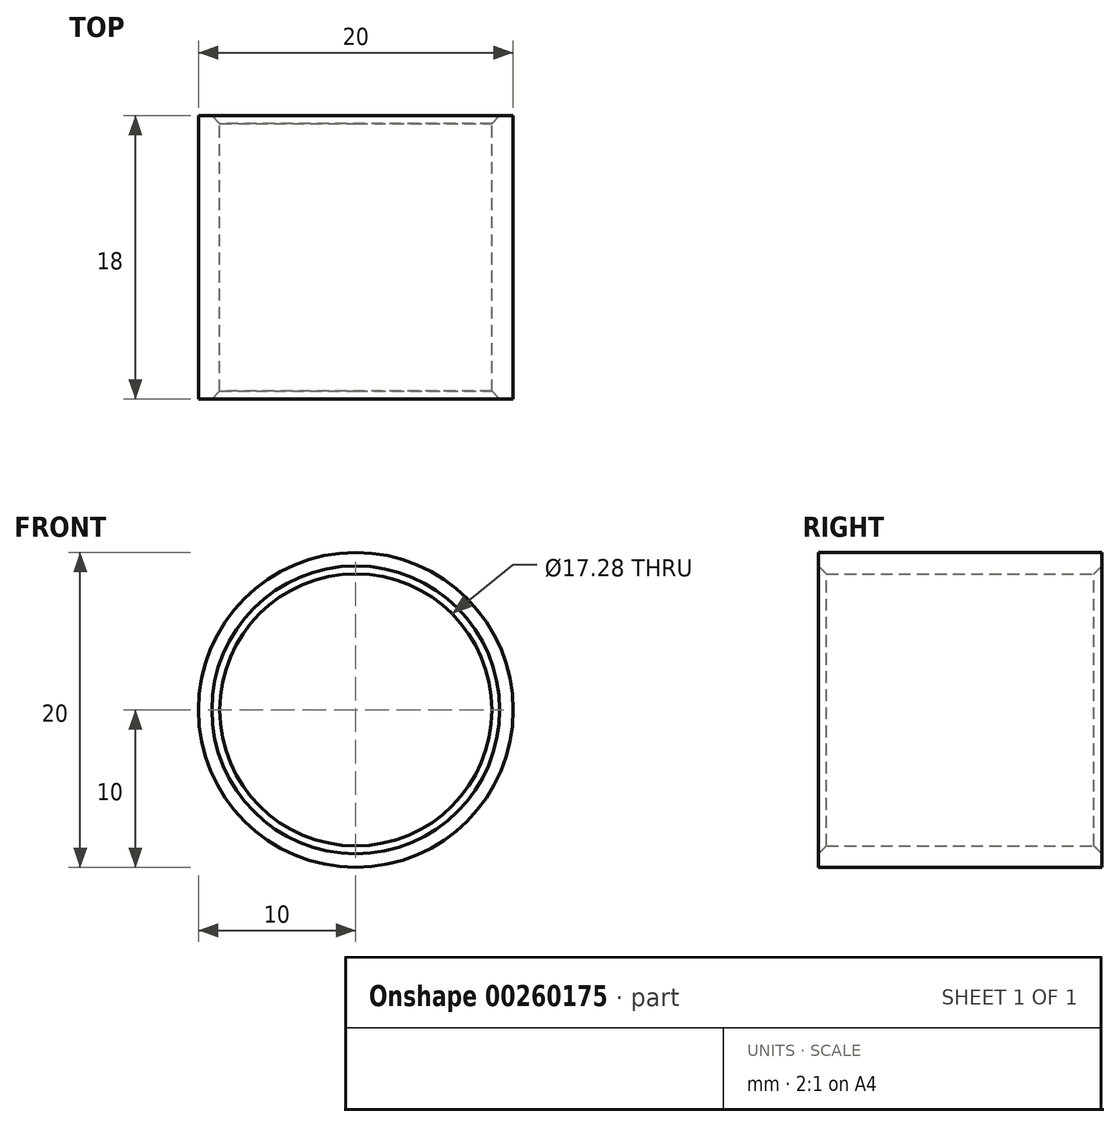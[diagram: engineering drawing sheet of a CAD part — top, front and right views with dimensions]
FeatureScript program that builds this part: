
annotation { "Feature Type Name" : "Feature", "Feature Type Description" : "" }
export const myFeature = defineFeature(function(context is Context, id is Id, definition is map)
    precondition{}
    {
        {
            var Q0;
            Q0=qCreatedBy(makeId("Front.planeOp"),FACE);
            var sketch = newSketch(context, id + "F0", { "sketchPlane" : qUnion([Q0])});
            skCircle(sketch, "E0", {"center": v(0, 0) * mm, "radius": 10 * mm});
            skCircle(sketch, "E1", {"center": v(0, 0) * mm, "radius": 8.64 * mm});
            skSolve(sketch);
        }
        {
            var Q0;
            Q0=makeQuery(id+"F0.imprint","IMPRINT",FACE,{"disambiguationData":[TD([[makeQuery(id+"F0.imprint","IMPRINT",EDGE,{"derivedFrom":sQuery(id+"F0.wireOp",EDGE,"E0")}),1.0]])]});
            extrude(context, id + "F1", {"entities" : qUnion([Q0]), "depth" : 18 * mm});
        }
        {
            var Q0;
            Q0=makeQuery(id+"F1.opExtrude","CAP_EDGE",EDGE,{"disambiguationData":[OSD([sQuery(id+"F0.wireOp",EDGE,"E1")])],"isStart":false});
            var Q1;
            Q1=makeQuery(id+"F1.opExtrude","CAP_EDGE",EDGE,{"disambiguationData":[OSD([sQuery(id+"F0.wireOp",EDGE,"E1")])],"isStart":true});
            chamfer(context, id + "F2", {"entities" : qUnion([Q0, Q1]), "width" : 0.5 * mm, "tangentPropagation" : true});
        }
    });
